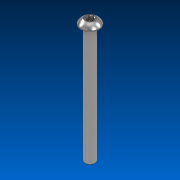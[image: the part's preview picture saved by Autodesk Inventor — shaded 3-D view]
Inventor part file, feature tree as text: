
AUTODESK INVENTOR PART (.ipt)
format: ipt  version: 2022.2 (Build 262287000, 287)  size: 162,304 bytes
history: native  units: in
note: dims shown in document units (in); Inventor stores cm internally (conversion verified against a paired STEP export)
features: direct_edit x1, chamfer x1, move_body x1
ambient origin geometry x8: Origin, YZ Plane, XZ Plane, XY Plane, X Axis, Y Axis, Z Axis, Center Point
bodies: Solid1 (feature_tree)
feature tree (3):
  direct_edit  "Direct Edit1"
  chamfer  "Chamfer2"  [1 undecoded]
  move_body  "Move1"
note: 1 required parameter value undecoded (feature->parameter linkage not recoverable at this tier; creation-order binding heuristic only, values carry confidence <= 0.55)
